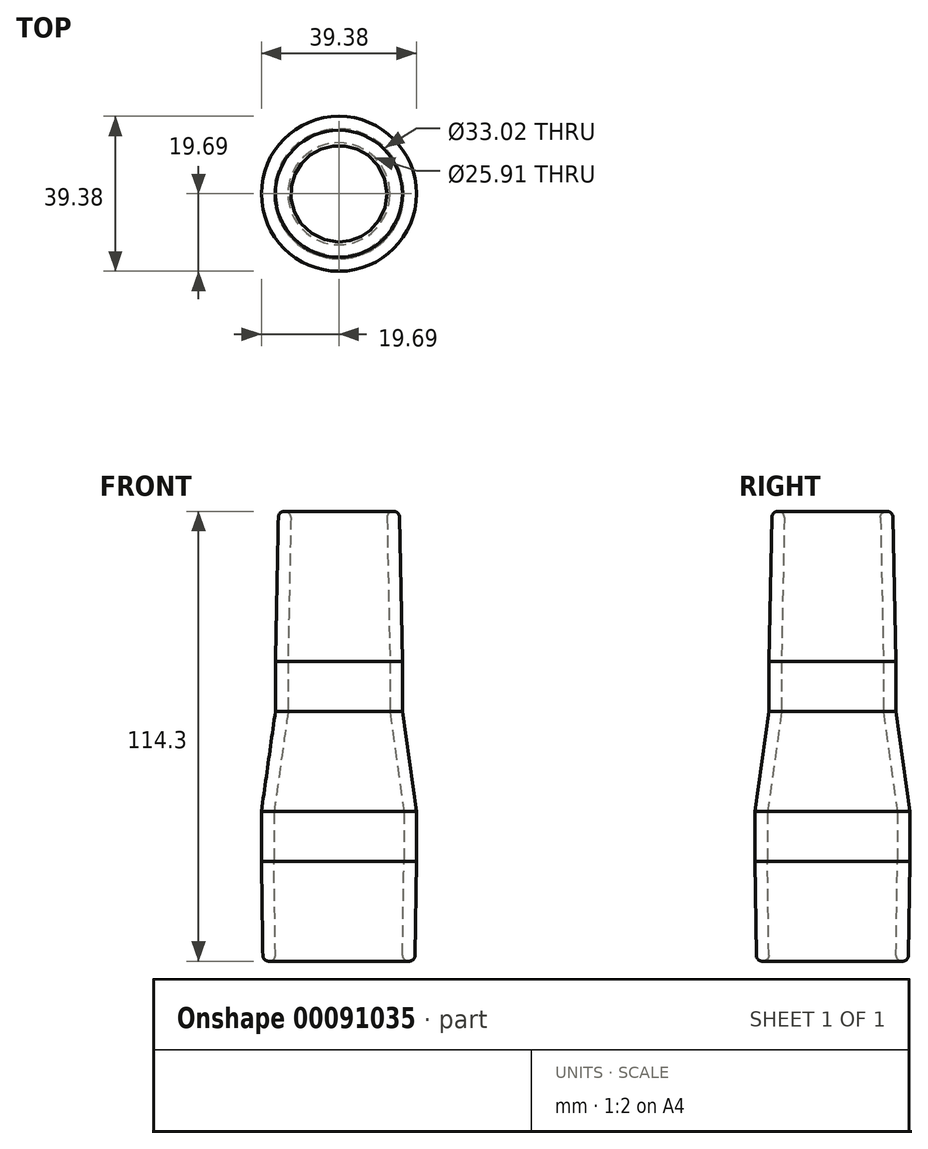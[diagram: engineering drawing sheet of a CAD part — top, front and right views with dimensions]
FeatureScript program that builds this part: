
annotation { "Feature Type Name" : "Feature", "Feature Type Description" : "" }
export const myFeature = defineFeature(function(context is Context, id is Id, definition is map)
    precondition{}
    {
        {
            var Q0;
            Q0=qCreatedBy(makeId("Front.planeOp"),FACE);
            var sketch = newSketch(context, id + "F0", { "sketchPlane" : qUnion([Q0])});
            skLineSegment(sketch, "E0", {"start": v(-19.3, 0) * mm, "end": v(-19.69, 25.4) * mm});
            skLineSegment(sketch, "E1", {"start": v(-19.69, 25.4) * mm, "end": v(-19.69, 38.1) * mm});
            skLineSegment(sketch, "E2", {"start": v(-19.69, 38.1) * mm, "end": v(-16.13, 63.5) * mm});
            skLineSegment(sketch, "E3", {"start": v(-16.13, 63.5) * mm, "end": v(-16.13, 76.2) * mm});
            skLineSegment(sketch, "E4", {"start": v(-16.13, 76.2) * mm, "end": v(-15.37, 114.3) * mm});
            skLineSegment(sketch, "E5", {"start": v(0, 0) * mm, "end": v(0, 121.02) * mm, "construction": true});
            skLineSegment(sketch, "E6.0", {"start": v(-12.95, 76.17) * mm, "end": v(-12.2, 114.3) * mm});
            skLineSegment(sketch, "E6.1", {"start": v(-16.13, 0) * mm, "end": v(-16.51, 25.42) * mm});
            skLineSegment(sketch, "E6.2", {"start": v(-16.51, 25.42) * mm, "end": v(-16.51, 37.88) * mm});
            skLineSegment(sketch, "E6.3", {"start": v(-16.51, 37.88) * mm, "end": v(-12.95, 63.28) * mm});
            skLineSegment(sketch, "E6.4", {"start": v(-12.95, 63.28) * mm, "end": v(-12.95, 76.17) * mm});
            skLineSegment(sketch, "E7", {"start": v(-15.37, 114.3) * mm, "end": v(-12.2, 114.3) * mm});
            skLineSegment(sketch, "E8", {"start": v(-16.13, 0) * mm, "end": v(-19.3, 0) * mm});
            skSolve(sketch);
        }
        {
            var Q0;
            Q0 = qSketchRegion(id + "F0", true);
            var Q1;
            Q1=sQuery(id+"F0.wireOp",EDGE,"E5");
            revolve(context, id + "F1", {"entities" : qUnion([Q0]), "axis" : qUnion([Q1]), "revolveType" : RevolveType.FULL});
        }
        {
            var Q0;
            Q0=makeQuery(id+"F1.opRevolve","SWEPT_EDGE",EDGE,{"disambiguationData":[OSD([sQuery(id+"F0.wireOp",EDGE,"E4"),sQuery(id+"F0.wireOp",EDGE,"E7")])]});
            var Q1;
            Q1=makeQuery(id+"F1.opRevolve","SWEPT_EDGE",EDGE,{"disambiguationData":[OSD([sQuery(id+"F0.wireOp",EDGE,"E6.0"),sQuery(id+"F0.wireOp",EDGE,"E7")])]});
            var Q2;
            Q2=makeQuery(id+"F1.opRevolve","SWEPT_EDGE",EDGE,{"disambiguationData":[OSD([sQuery(id+"F0.wireOp",EDGE,"E0"),sQuery(id+"F0.wireOp",EDGE,"E8")])]});
            var Q3;
            Q3=makeQuery(id+"F1.opRevolve","SWEPT_EDGE",EDGE,{"disambiguationData":[OSD([sQuery(id+"F0.wireOp",EDGE,"E6.1"),sQuery(id+"F0.wireOp",EDGE,"E8")])]});
            fillet(context, id + "F2", {"entities" : qUnion([Q0, Q1, Q2, Q3]), "radius" : 1.52 * mm, "tangentPropagation" : true, "allowEdgeOverflow" : false});
        }
    });
